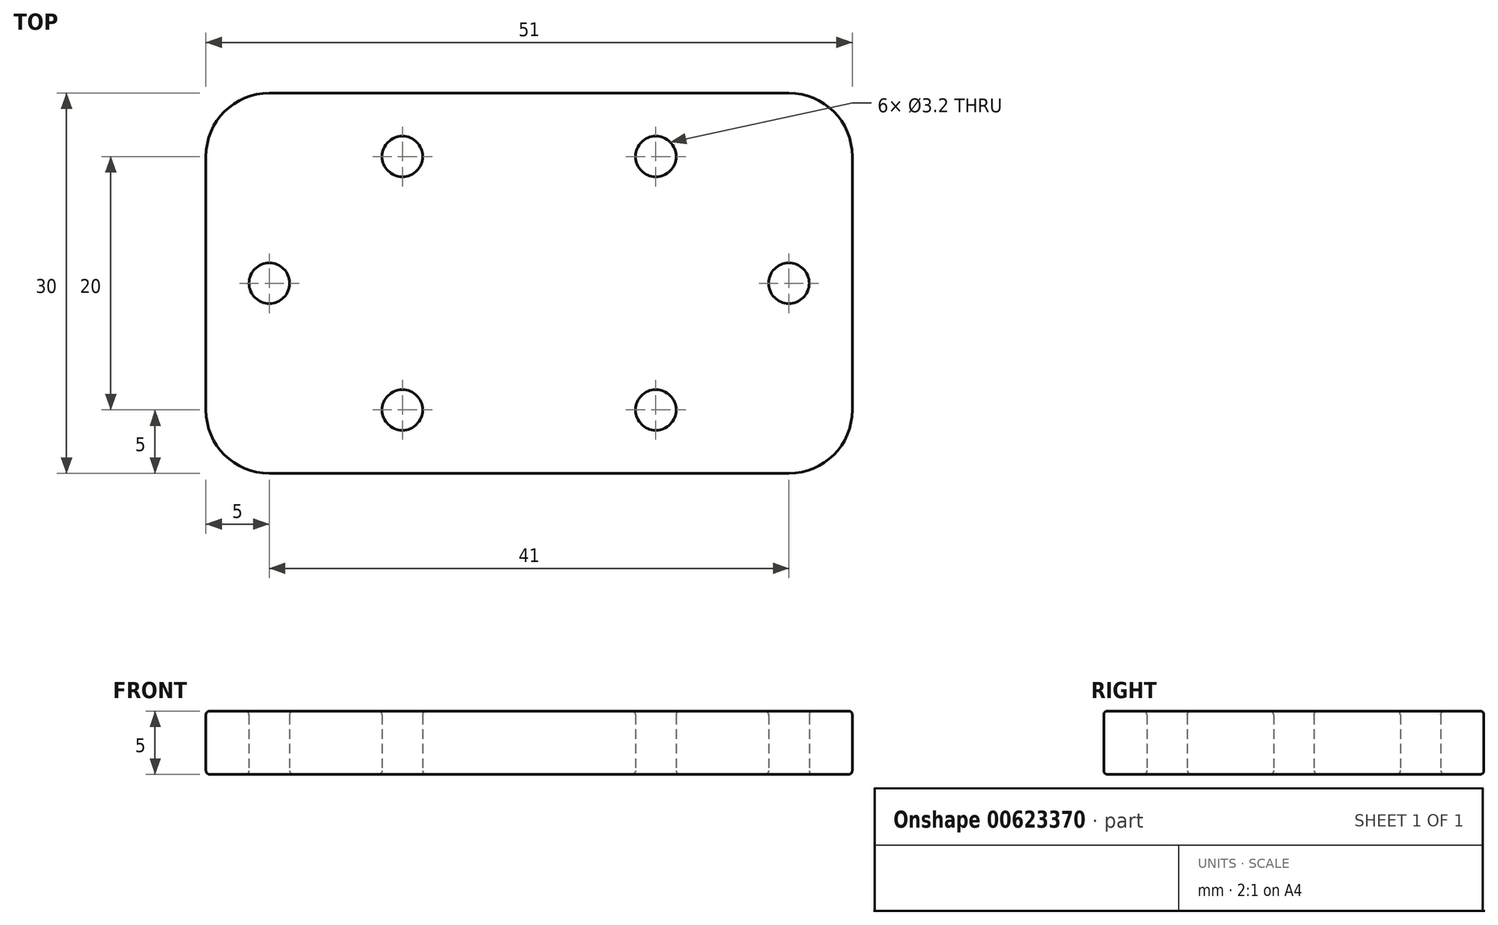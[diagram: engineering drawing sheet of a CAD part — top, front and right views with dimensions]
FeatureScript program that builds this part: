
annotation { "Feature Type Name" : "Feature", "Feature Type Description" : "" }
export const myFeature = defineFeature(function(context is Context, id is Id, definition is map)
    precondition{}
    {
        {
            var Q0;
            Q0=qCreatedBy(makeId("Top.planeOp"),FACE);
            var sketch = newSketch(context, id + "F0", { "sketchPlane" : qUnion([Q0])});
            skCircle(sketch, "E0", {"center": v(0, 0) * mm, "radius": 1.6 * mm});
            skCircle(sketch, "E1", {"center": v(41, 0) * mm, "radius": 1.6 * mm});
            skLineSegment(sketch, "E2", {"start": v(0, 0) * mm, "end": v(41, 0) * mm, "construction": true});
            skLineSegment(sketch, "E3", {"start": v(20.5, 0) * mm, "end": v(20.5, 10) * mm, "construction": true});
            skLineSegment(sketch, "E4", {"start": v(20.5, 10) * mm, "end": v(10.5, 10) * mm, "construction": true});
            skCircle(sketch, "E5", {"center": v(10.5, 10) * mm, "radius": 1.6 * mm});
            skCircle(sketch, "E6.MirrorC", {"center": v(30.5, 10) * mm, "radius": 1.6 * mm});
            skCircle(sketch, "E7.MirrorC", {"center": v(30.5, -10) * mm, "radius": 1.6 * mm});
            skCircle(sketch, "E8.MirrorC", {"center": v(10.5, -10) * mm, "radius": 1.6 * mm});
            skLineSegment(sketch, "E9.bottom", {"start": v(46, 15) * mm, "end": v(-5, 15) * mm});
            skLineSegment(sketch, "E9.top", {"start": v(46, -15) * mm, "end": v(-5, -15) * mm});
            skLineSegment(sketch, "E9.left", {"start": v(46, 15) * mm, "end": v(46, -15) * mm});
            skLineSegment(sketch, "E9.right", {"start": v(-5, 15) * mm, "end": v(-5, -15) * mm});
            skPoint(sketch, "E9.middle", {"position": v(20.5, 0) * mm});
            skSolve(sketch);
        }
        {
            var Q0;
            Q0=makeQuery(id+"F0.imprint","IMPRINT",FACE,{"disambiguationData":[TD([[makeQuery(id+"F0.imprint","IMPRINT",EDGE,{"derivedFrom":sQuery(id+"F0.wireOp",EDGE,"E0")}),-1.0]])]});
            extrude(context, id + "F1", {"entities" : qUnion([Q0]), "depth" : 5 * mm, "offsetDistance" : 25 * mm});
        }
        {
            var Q0;
            Q0=makeQuery(id+"F1.opExtrude","SWEPT_EDGE",EDGE,{"disambiguationData":[OSD([sQuery(id+"F0.wireOp",EDGE,"E9.top"),sQuery(id+"F0.wireOp",EDGE,"E9.right")])]});
            var Q1;
            Q1=makeQuery(id+"F1.opExtrude","SWEPT_EDGE",EDGE,{"disambiguationData":[OSD([sQuery(id+"F0.wireOp",EDGE,"E9.top"),sQuery(id+"F0.wireOp",EDGE,"E9.left")])]});
            var Q2;
            Q2=makeQuery(id+"F1.opExtrude","SWEPT_EDGE",EDGE,{"disambiguationData":[OSD([sQuery(id+"F0.wireOp",EDGE,"E9.bottom"),sQuery(id+"F0.wireOp",EDGE,"E9.left")])]});
            var Q3;
            Q3=makeQuery(id+"F1.opExtrude","SWEPT_EDGE",EDGE,{"disambiguationData":[OSD([sQuery(id+"F0.wireOp",EDGE,"E9.bottom"),sQuery(id+"F0.wireOp",EDGE,"E9.right")])]});
            fillet(context, id + "F2", {"entities" : qUnion([Q0, Q1, Q2, Q3]), "radius" : 5 * mm, "tangentPropagation" : true, "allowEdgeOverflow" : false});
        }
        {
            var Q0;
            Q0=makeQuery(id+"F1.opExtrude","CAP_FACE",FACE,{"disambiguationData":[OSD([sQuery(id+"F0.wireOp",EDGE,"E0"),sQuery(id+"F0.wireOp",EDGE,"E1"),sQuery(id+"F0.wireOp",EDGE,"E5"),sQuery(id+"F0.wireOp",EDGE,"E6.MirrorC"),sQuery(id+"F0.wireOp",EDGE,"E7.MirrorC"),sQuery(id+"F0.wireOp",EDGE,"E8.MirrorC"),sQuery(id+"F0.wireOp",EDGE,"E9.bottom"),sQuery(id+"F0.wireOp",EDGE,"E9.top"),sQuery(id+"F0.wireOp",EDGE,"E9.left"),sQuery(id+"F0.wireOp",EDGE,"E9.right")])],"isStart":true});
            var Q1;
            Q1=makeQuery(id+"F1.opExtrude","CAP_FACE",FACE,{"disambiguationData":[OSD([sQuery(id+"F0.wireOp",EDGE,"E0"),sQuery(id+"F0.wireOp",EDGE,"E1"),sQuery(id+"F0.wireOp",EDGE,"E5"),sQuery(id+"F0.wireOp",EDGE,"E6.MirrorC"),sQuery(id+"F0.wireOp",EDGE,"E7.MirrorC"),sQuery(id+"F0.wireOp",EDGE,"E8.MirrorC"),sQuery(id+"F0.wireOp",EDGE,"E9.bottom"),sQuery(id+"F0.wireOp",EDGE,"E9.top"),sQuery(id+"F0.wireOp",EDGE,"E9.left"),sQuery(id+"F0.wireOp",EDGE,"E9.right")])],"isStart":false});
            fillet(context, id + "F3", {"entities" : qUnion([Q0, Q1]), "radius" : 0.3 * mm, "tangentPropagation" : true, "allowEdgeOverflow" : false});
        }
    });
